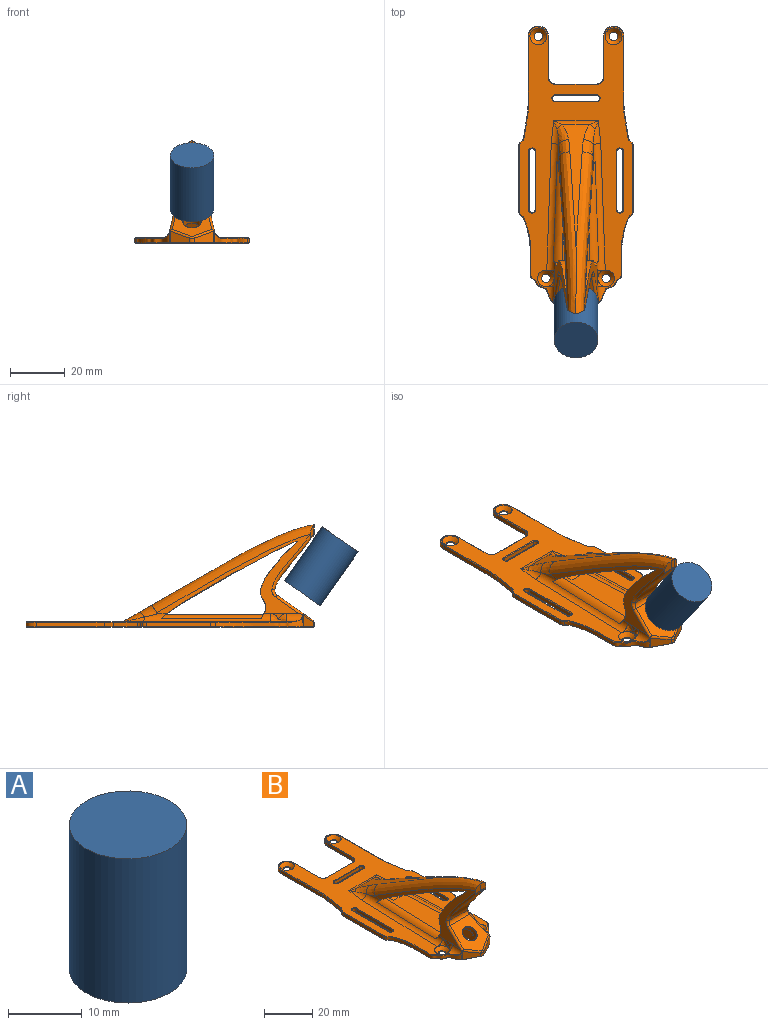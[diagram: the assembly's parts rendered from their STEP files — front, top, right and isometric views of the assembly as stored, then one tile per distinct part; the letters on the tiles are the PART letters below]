
ASSEMBLY  parts=2 mates=1
PART A: 3 faces, bbox 16x16x24 mm
  f0: cylinder r=8mm len=24mm, axis (0,0,-1), area 1206.4mm2, adj f1,f2
  f1: plane 16x16mm, normal (0,0,1), area 201.1mm2, adj f0
  f2: plane 16x16mm, normal (0,0,-1), area 201.1mm2, adj f0
PART B: 226 faces, bbox 42.2x106.4x37.8 mm
  f0: plane 104.85x41.61mm, normal (0,0,-1), area 2882.3mm2, adj f116,f117,f118,f119,f120,f121,f122,f123
  f1: plane 6.09x2.05mm, normal (-1,0.04,0), area 3.8mm2, adj f6,f85
  f2: plane 6.09x2.05mm, normal (1,0.04,0), area 3.8mm2, adj f5,f79
  f3: plane 4.72x2.47mm, normal (-0.46,-0.89,0), area 7mm2, adj f6,f7,f96,f102,f103
  f4: plane 4.71x2.46mm, normal (0.46,-0.89,0), area 7mm2, adj f5,f7,f95,f108,f110
  f5: plane 56.16x28.95mm, normal (0.98,0.03,0.17), area 222.2mm2, adj f2,f4,f76,f77,f78,f80,f94,f95
  f6: plane 56.16x28.95mm, normal (-0.98,0.03,0.17), area 222.2mm2, adj f1,f3,f76,f77,f83,f86,f96,f97
  f7: cylinder r=2mm len=3.6mm, axis (0,0,1), area 6.6mm2, adj f3,f4,f95,f96,f105
  f8: plane 7.11x4.16mm, normal (-0.46,-0.89,0), area 23mm2, adj f61,f62,f109,f150
  f9: plane 7.11x4.16mm, normal (0.46,-0.89,0), area 23mm2, adj f61,f63,f113,f154
  f10: cylinder r=3.15mm len=6.54mm, axis (0,0.57,-0.82), area 47.6mm2, adj f53,f225
  f11: cylinder r=1.1mm len=2.2mm, axis (0,0,-1), area 5.5mm2, adj f12,f45,f173,f222
  f12: plane 15x1.6mm, normal (0,-1,0), area 24mm2, adj f11,f13,f172,f224
  f13: cylinder r=1.1mm len=2.2mm, axis (0,0,-1), area 5.5mm2, adj f12,f45,f174,f223
  f14: cylinder r=1.1mm len=2.2mm, axis (0,0,-1), area 5.5mm2, adj f15,f40,f164,f219
  f15: plane 21.23x1.6mm, normal (1,0,0), area 34mm2, adj f14,f16,f166,f217
  f16: cylinder r=1.1mm len=2.2mm, axis (0,0,-1), area 5.5mm2, adj f15,f40,f167,f218
  f17: cylinder r=1.1mm len=2.2mm, axis (0,0,-1), area 5.5mm2, adj f18,f42,f169,f214
  f18: plane 21.23x1.6mm, normal (-1,0,0), area 34mm2, adj f17,f19,f168,f213
  f19: cylinder r=1.1mm len=2.2mm, axis (0,0,-1), area 5.5mm2, adj f18,f42,f170,f215
  f20: extruded ~32.1x12mm, area 64.2mm2, adj f63,f66,f157,f181,f182
  f21: plane 23.55x1.6mm, normal (1,0,0), area 37.7mm2, adj f66,f67,f153,f184
  f22: plane 1.6x0.89mm, normal (0.74,0.68,0), area 1.9mm2, adj f67,f73,f149,f186
  f23: plane 8.71x1.6mm, normal (0.99,0.16,0), area 14.1mm2, adj f69,f73,f145,f188
  f24: plane 3.14x1.6mm, normal (1,0.08,0), area 5mm2, adj f69,f70,f141,f190
  f25: plane 24.78x1.6mm, normal (1,0,0), area 39.7mm2, adj f26,f70,f137,f192
  f26: cylinder r=3.75mm len=7.5mm, axis (0,0,-1), area 18.8mm2, adj f25,f27,f135,f193
  f27: plane 14.86x1.6mm, normal (-1,0,0), area 23.8mm2, adj f26,f28,f133,f194
  f28: cylinder r=2.61mm len=2.61mm, axis (0,0,-1), area 6.6mm2, adj f27,f29,f131,f195
  f29: plane 14.78x1.6mm, normal (0,1,0), area 23.7mm2, adj f28,f30,f129,f196
  f30: cylinder r=2.61mm len=2.61mm, axis (0,0,-1), area 6.6mm2, adj f29,f31,f127,f197
  f31: plane 14.86x1.6mm, normal (1,0,0), area 23.8mm2, adj f30,f32,f125,f198
  f32: cylinder r=3.75mm len=7.5mm, axis (0,0,-1), area 18.8mm2, adj f31,f33,f124,f199
  f33: plane 24.78x1.6mm, normal (-1,0,0), area 39.7mm2, adj f32,f71,f126,f200
  f34: plane 3.14x1.6mm, normal (-1,0.08,0), area 5mm2, adj f71,f72,f130,f202
  f35: plane 8.71x1.6mm, normal (-0.99,0.16,0), area 14.1mm2, adj f68,f72,f134,f204
  f36: plane 1.6x0.89mm, normal (-0.74,0.68,0), area 1.9mm2, adj f64,f68,f138,f206
  f37: plane 23.55x1.6mm, normal (-1,0,0), area 37.7mm2, adj f64,f65,f142,f208
  f38: cylinder r=1.57mm len=3.15mm, axis (0,0,-1), area 3mm2, adj f59,f177
  f39: cylinder r=1.57mm len=3.15mm, axis (0,0,-1), area 3mm2, adj f58,f176
  f40: plane 21.23x1.6mm, normal (-1,0,0), area 34mm2, adj f14,f16,f165,f220
  f41: cylinder r=1.55mm len=3.1mm, axis (0,0,-1), area 2.9mm2, adj f56,f178
  f42: plane 21.23x1.6mm, normal (1,0,0), area 34mm2, adj f17,f19,f171,f216
  f43: cylinder r=1.55mm len=3.1mm, axis (0,0,-1), area 2.9mm2, adj f57,f179
  f44: extruded ~32.1x12mm, area 64.2mm2, adj f62,f65,f146,f210,f211
  f45: plane 15x1.6mm, normal (0,1,0), area 24mm2, adj f11,f13,f175,f221
  f46: plane 96x41.6mm, normal (0,0,1), area 1596.5mm2, adj f56,f57,f58,f59,f78,f80,f81,f82
  f47: plane 8.66x7.62mm, normal (0.87,-0.41,-0.29), area 37mm2, adj f48,f52,f53,f162,f163
  f48: plane 7.68x5.38mm, normal (0,-0.82,-0.57), area 43.9mm2, adj f47,f49,f53,f159,f161,f163
  f49: plane 8.66x7.62mm, normal (-0.87,-0.41,-0.29), area 37mm2, adj f48,f50,f53,f158,f159
  f50: plane 6.95x5.18mm, normal (-0.87,0.41,0.29), area 23mm2, adj f49,f51,f53,f158,f160
  f51: plane 4.69x2.79mm, normal (0,0.82,0.57), area 16mm2, adj f50,f52,f53,f160
  f52: plane 6.95x5.18mm, normal (0.87,0.41,0.29), area 23mm2, adj f47,f51,f53,f160,f162
  f53: plane 9.38x6.65mm, normal (0,0.57,-0.82), area 25.9mm2, adj f10,f47,f48,f49,f50,f51,f52
  f54: extruded ~19.58x13.98mm, area 169.4mm2, adj f60,f102,f103,f105,f108,f110
  f55: plane 14.42x13.09mm, normal (0,-0.57,0.82), area 147mm2, adj f60,f107,f109,f111,f113,f114,f225
  f56: cone r=1.55mm half-angle=45deg, axis (0,0,1), area 30.7mm2, adj f41,f46,f79
  f57: cone r=1.55mm half-angle=45deg, axis (0,0,1), area 30.7mm2, adj f43,f46,f85
  f58: cone r=3.08mm half-angle=45deg, axis (0,0,1), area 31mm2, adj f39,f46
  f59: cone r=1.57mm half-angle=45deg, axis (0,0,1), area 31mm2, adj f38,f46
  f60: cylinder r=2mm len=11.41mm, axis (1,0,0), area 23.5mm2, adj f54,f55,f104,f112
  f61: cylinder r=2mm len=1.84mm, axis (0,0,1), area 3mm2, adj f8,f9,f111,f152
  f62: cylinder r=2mm len=4.16mm, axis (0,0,-1), area 1.2mm2, adj f8,f44,f106,f148,f212
  f63: cylinder r=2mm len=4.16mm, axis (0,0,-1), area 1.2mm2, adj f9,f20,f115,f156,f180
  f64: cylinder r=2mm len=1.6mm, axis (0,0,1), area 2.4mm2, adj f36,f37,f140,f207
  f65: cylinder r=2mm len=1.6mm, axis (0,0,-1), area 2.8mm2, adj f37,f44,f144,f209
  f66: cylinder r=2mm len=1.6mm, axis (0,0,-1), area 2.8mm2, adj f20,f21,f155,f183
  f67: cylinder r=2mm len=1.6mm, axis (0,0,-1), area 2.4mm2, adj f21,f22,f151,f185
  f68: cylinder r=2mm len=1.6mm, axis (0,0,1), area 1.9mm2, adj f35,f36,f136,f205
  f69: cylinder r=2mm len=1.6mm, axis (0,0,1), area 0.3mm2, adj f23,f24,f143,f189
  f70: cylinder r=2mm len=1.6mm, axis (0,0,1), area 0.2mm2, adj f24,f25,f139,f191
  f71: cylinder r=2mm len=1.6mm, axis (0,0,1), area 0.2mm2, adj f33,f34,f128,f201
  f72: cylinder r=2mm len=1.6mm, axis (0,0,1), area 0.3mm2, adj f34,f35,f132,f203
  f73: cylinder r=2mm len=1.6mm, axis (0,0,1), area 1.9mm2, adj f22,f23,f147,f187
  f74: extruded ~44.51x25.33mm, area 163.2mm2, adj f82,f93,f94,f95,f96,f97,f98
  f75: plane 35.61x10.28mm, normal (0,0,1), area 300.5mm2, adj f76,f77,f88,f90,f91,f100,f101
  f76: extruded ~28.33x16.46mm, area 345mm2, adj f5,f6,f75,f77,f80,f86,f100,f101
  f77: extruded ~49.67x28.33mm, area 519.4mm2, adj f5,f6,f75,f76,f80,f86,f89,f90
  f78: cylinder r=3mm len=5.88mm, axis (-0.04,1,0), area 19.9mm2, adj f5,f46,f79,f114,f180,f181
  f79: bspline ~6.79x3.25mm, area 16.8mm2, adj f2,f56,f78,f80
  f80: cylinder r=3mm len=46.28mm, axis (-0.04,1,0), area 141mm2, adj f5,f46,f76,f77,f79,f81,f94,f100
  f81: cylinder r=3mm len=8.78mm, axis (-0.11,0.99,0), area 16.2mm2, adj f46,f80,f92,f93,f94
  f82: cylinder r=3mm len=16.24mm, axis (1,0,0), area 19.6mm2, adj f46,f74,f92,f99
  f83: cylinder r=3mm len=5.88mm, axis (-0.04,-1,0), area 19.9mm2, adj f6,f46,f85,f107,f211,f212
  f84: cylinder r=3mm len=8.78mm, axis (-0.11,-0.99,0), area 16.2mm2, adj f46,f86,f97,f98,f99
  f85: bspline ~6.79x3.25mm, area 16.8mm2, adj f1,f57,f83,f86
  f86: cylinder r=3mm len=46.28mm, axis (-0.04,-1,0), area 141mm2, adj f6,f46,f76,f77,f84,f85,f97,f101
  f87: cylinder r=3.77mm len=7.52mm, axis (1,0,0), area 57mm2, adj f90,f91,f119,f123
  f88: cylinder r=5.77mm len=5.01mm, axis (1,0,0), area 25.8mm2, adj f75,f90,f91,f120,f121,f122
  f89: cylinder r=5.77mm len=6.38mm, axis (1,0,0), area 47.4mm2, adj f77,f90,f91,f116,f117,f118
  f90: plane 11.52x5.57mm, normal (1,0,0), area 26.4mm2, adj f75,f77,f87,f88,f89,f117,f119,f122
  f91: plane 11.52x5.57mm, normal (-1,0,0), area 26.4mm2, adj f75,f77,f87,f88,f89,f118,f119,f121
  f92: bspline ~3.82x3.65mm, area 2.5mm2, adj f81,f82,f93
  f93: bspline ~9.06x4.61mm, area 21.9mm2, adj f74,f81,f92,f94
  f94: bspline ~9.19x5.76mm, area 26.3mm2, adj f5,f74,f80,f81,f93,f95
  f95: bspline ~61.44x33.07mm, area 351mm2, adj f4,f5,f7,f74,f94,f96
  f96: bspline ~64.06x34.52mm, area 351mm2, adj f3,f6,f7,f74,f95,f97
  f97: bspline ~9.19x5.76mm, area 26.3mm2, adj f6,f74,f84,f86,f96,f98
  f98: bspline ~9.06x4.61mm, area 21.9mm2, adj f74,f84,f97,f99
  f99: bspline ~3.82x3.65mm, area 2.5mm2, adj f82,f84,f98
  f100: cylinder r=4mm len=37.15mm, axis (-0.04,1,0), area 128.4mm2, adj f75,f76,f77,f80
  f101: cylinder r=4mm len=37.15mm, axis (-0.04,-1,0), area 128.4mm2, adj f75,f76,f77,f86
  f102: bspline ~21.26x15.46mm, area 40.2mm2, adj f3,f6,f54,f103,f104
  f103: bspline ~5.15x3.44mm, area 2mm2, adj f3,f54,f102,f105
  f104: bspline ~2.81x1.89mm, area 4mm2, adj f6,f60,f102,f107
  f105: bspline ~2.6x0.93mm, area 1.2mm2, adj f7,f54,f103,f108
  f106: bspline ~0.3x0.17mm, area 0mm2, adj f62,f107,f109,f212
  f107: cylinder r=1mm len=10.49mm, axis (-0.13,-0.81,-0.57), area 17mm2, adj f6,f55,f83,f104,f106,f109,f212
  f108: bspline ~5.15x3.44mm, area 2mm2, adj f4,f54,f105,f110
  f109: cylinder r=1mm len=7.57mm, axis (-0.84,0.44,0.31), area 8.6mm2, adj f8,f55,f106,f107,f111
  f110: bspline ~21.26x15.46mm, area 40.2mm2, adj f4,f5,f54,f108,f112
  f111: bspline ~1.84x0.9mm, area 1.5mm2, adj f55,f61,f109,f113
  f112: bspline ~2.81x1.89mm, area 4mm2, adj f5,f60,f110,f114
  f113: cylinder r=1mm len=7.57mm, axis (-0.84,-0.44,-0.31), area 8.6mm2, adj f9,f55,f111,f114,f115
  f114: cylinder r=1mm len=10.49mm, axis (0.13,-0.81,-0.57), area 17mm2, adj f5,f55,f78,f112,f113,f115,f180
  f115: bspline ~0.3x0.17mm, area 0mm2, adj f63,f113,f114,f180
  f116: plane 5.4x0.2mm, normal (0,-0.7,-0.72), area 1.4mm2, adj f0,f89,f117,f118
  f117: plane 2.4x0.2mm, normal (0.71,0,-0.71), area 0.6mm2, adj f0,f89,f90,f116,f119
  f118: plane 2.4x0.2mm, normal (-0.71,0,-0.71), area 0.6mm2, adj f0,f89,f91,f116,f119
  f119: plane 5.4x0.21mm, normal (0,0.73,-0.69), area 1.5mm2, adj f0,f87,f90,f91,f117,f118
  f120: plane 5.4x0.2mm, normal (0,0.7,-0.72), area 1.4mm2, adj f0,f88,f121,f122
  f121: plane 2.4x0.2mm, normal (-0.71,0,-0.71), area 0.6mm2, adj f0,f88,f91,f120,f123
  f122: plane 2.4x0.2mm, normal (0.71,0,-0.71), area 0.6mm2, adj f0,f88,f90,f120,f123
  f123: plane 5.4x0.21mm, normal (0,-0.73,-0.69), area 1.5mm2, adj f0,f87,f90,f91,f121,f122
  f124: cone r=3.75mm half-angle=45deg, axis (0,0,1), area 3.2mm2, adj f0,f32,f125,f126
  f125: plane 14.86x0.2mm, normal (0.71,0,-0.71), area 4.2mm2, adj f0,f31,f124,f127
  f126: plane 24.78x0.2mm, normal (-0.71,0,-0.71), area 7mm2, adj f0,f33,f124,f128
  f127: cone r=2.81mm half-angle=45deg, axis (0,0,-1), area 1.2mm2, adj f0,f30,f125,f129
  f128: cone r=2.2mm half-angle=45deg, axis (0,0,-1), area 0mm2, adj f0,f71,f126,f130
  f129: plane 14.78x0.2mm, normal (0,0.71,-0.71), area 4.2mm2, adj f0,f29,f127,f131
  f130: plane 3.16x0.44mm, normal (-0.71,0.05,-0.71), area 0.9mm2, adj f0,f34,f128,f132
  f131: cone r=2.81mm half-angle=45deg, axis (0,0,-1), area 1.2mm2, adj f0,f28,f129,f133
  f132: cone r=2.2mm half-angle=45deg, axis (0,0,-1), area 0mm2, adj f0,f72,f130,f134
  f133: plane 14.86x0.2mm, normal (-0.71,0,-0.71), area 4.2mm2, adj f0,f27,f131,f135
  f134: plane 8.74x1.58mm, normal (-0.7,0.11,-0.71), area 2.5mm2, adj f0,f35,f132,f136
  f135: cone r=3.55mm half-angle=45deg, axis (0,0,1), area 3.2mm2, adj f0,f26,f133,f137
  f136: cone r=2.2mm half-angle=45deg, axis (0,0,-1), area 0.3mm2, adj f0,f68,f134,f138
  f137: plane 24.78x0.2mm, normal (0.71,0,-0.71), area 7mm2, adj f0,f25,f135,f139
  f138: plane 1.02x0.96mm, normal (-0.52,0.48,-0.71), area 0.3mm2, adj f0,f36,f136,f140
  f139: cone r=2.2mm half-angle=45deg, axis (0,0,-1), area 0mm2, adj f0,f70,f137,f141
  f140: cone r=1.8mm half-angle=45deg, axis (0,0,1), area 0.4mm2, adj f0,f64,f138,f142
  f141: plane 3.16x0.44mm, normal (0.71,0.05,-0.71), area 0.9mm2, adj f0,f24,f139,f143
  f142: plane 23.55x0.2mm, normal (-0.71,0,-0.71), area 6.7mm2, adj f0,f37,f140,f144
  f143: cone r=2.2mm half-angle=45deg, axis (0,0,-1), area 0mm2, adj f0,f69,f141,f145
  f144: cone r=1.8mm half-angle=45deg, axis (0,0,1), area 0.5mm2, adj f0,f65,f142,f146
  f145: plane 8.74x1.58mm, normal (0.7,0.11,-0.71), area 2.5mm2, adj f0,f23,f143,f147
  f146: bspline ~32.26x12.12mm, area 10.3mm2, adj f0,f44,f144,f148
  f147: cone r=2.2mm half-angle=45deg, axis (0,0,-1), area 0.3mm2, adj f0,f73,f145,f149
  f148: cone r=1.8mm half-angle=45deg, axis (0,0,1), area 0.1mm2, adj f0,f62,f146,f150
  f149: plane 1.02x0.96mm, normal (0.52,0.48,-0.71), area 0.3mm2, adj f0,f22,f147,f151
  f150: plane 7.2x3.87mm, normal (-0.33,-0.63,-0.71), area 2.3mm2, adj f0,f8,f148,f152
  f151: cone r=1.8mm half-angle=45deg, axis (0,0,1), area 0.4mm2, adj f0,f67,f149,f153
  f152: cone r=1.8mm half-angle=45deg, axis (0,0,1), area 0.5mm2, adj f0,f61,f150,f154
  f153: plane 23.55x0.2mm, normal (0.71,0,-0.71), area 6.7mm2, adj f0,f21,f151,f155
  f154: plane 7.2x3.87mm, normal (0.33,-0.63,-0.71), area 2.3mm2, adj f0,f9,f152,f156
  f155: cone r=1.8mm half-angle=45deg, axis (0,0,1), area 0.5mm2, adj f0,f66,f153,f157
  f156: cone r=1.8mm half-angle=45deg, axis (0,0,1), area 0.1mm2, adj f0,f63,f154,f157
  f157: bspline ~32.26x12.12mm, area 10.3mm2, adj f0,f20,f155,f156
  f158: plane 5.2x2.61mm, normal (-0.73,0.34,-0.6), area 1.8mm2, adj f0,f49,f50,f159,f160
  f159: plane 5.3x2.58mm, normal (-0.54,-0.26,-0.8), area 1.4mm2, adj f0,f48,f49,f158,f161
  f160: plane 4.92x0.31mm, normal (0,0.89,-0.46), area 1.7mm2, adj f0,f50,f51,f52,f158,f162
  f161: plane 4.92x0.16mm, normal (0,-0.46,-0.89), area 0.9mm2, adj f0,f48,f159,f163
  f162: plane 5.2x2.61mm, normal (0.73,0.34,-0.6), area 1.8mm2, adj f0,f47,f52,f160,f163
  f163: plane 5.3x2.58mm, normal (0.54,-0.26,-0.8), area 1.4mm2, adj f0,f47,f48,f161,f162
  f164: cone r=1.3mm half-angle=45deg, axis (0,0,-1), area 1.1mm2, adj f0,f14,f165,f166
  f165: plane 21.23x0.2mm, normal (-0.71,0,-0.71), area 6mm2, adj f0,f40,f164,f167
  f166: plane 21.23x0.2mm, normal (0.71,0,-0.71), area 6mm2, adj f0,f15,f164,f167
  f167: cone r=1.3mm half-angle=45deg, axis (0,0,-1), area 1.1mm2, adj f0,f16,f165,f166
  f168: plane 21.23x0.2mm, normal (-0.71,0,-0.71), area 6mm2, adj f0,f18,f169,f170
  f169: cone r=1.1mm half-angle=45deg, axis (0,0,-1), area 1.1mm2, adj f0,f17,f168,f171
  f170: cone r=1.1mm half-angle=45deg, axis (0,0,-1), area 1.1mm2, adj f0,f19,f168,f171
  f171: plane 21.23x0.2mm, normal (0.71,0,-0.71), area 6mm2, adj f0,f42,f169,f170
  f172: plane 15x0.2mm, normal (0,-0.71,-0.71), area 4.2mm2, adj f0,f12,f173,f174
  f173: cone r=1.1mm half-angle=45deg, axis (0,0,-1), area 1.1mm2, adj f0,f11,f172,f175
  f174: cone r=1.1mm half-angle=45deg, axis (0,0,-1), area 1.1mm2, adj f0,f13,f172,f175
  f175: plane 15x0.2mm, normal (0,0.71,-0.71), area 4.2mm2, adj f0,f45,f173,f174
  f176: cone r=1.57mm half-angle=45deg, axis (0,0,-1), area 3mm2, adj f0,f39
  f177: cone r=1.78mm half-angle=45deg, axis (0,0,-1), area 3mm2, adj f0,f38
  f178: cone r=1.75mm half-angle=45deg, axis (0,0,-1), area 2.9mm2, adj f0,f41
  f179: cone r=1.75mm half-angle=45deg, axis (0,0,-1), area 2.9mm2, adj f0,f43
  f180: bspline ~0.82x0.33mm, area 0.2mm2, adj f63,f78,f114,f115,f181
  f181: bspline ~4.97x2.79mm, area 1.4mm2, adj f20,f78,f180,f182
  f182: bspline ~27.42x9.35mm, area 8.7mm2, adj f20,f46,f181,f183
  f183: cone r=1.8mm half-angle=45deg, axis (0,0,-1), area 0.5mm2, adj f46,f66,f182,f184
  f184: plane 23.55x0.2mm, normal (0.71,0,0.71), area 6.7mm2, adj f21,f46,f183,f185
  f185: cone r=1.8mm half-angle=45deg, axis (0,0,-1), area 0.4mm2, adj f46,f67,f184,f186
  f186: plane 1.02x0.96mm, normal (0.52,0.48,0.71), area 0.3mm2, adj f22,f46,f185,f187
  f187: cone r=2.2mm half-angle=45deg, axis (0,0,1), area 0.3mm2, adj f46,f73,f186,f188
  f188: plane 8.74x1.58mm, normal (0.7,0.11,0.71), area 2.5mm2, adj f23,f46,f187,f189
  f189: cone r=2.2mm half-angle=45deg, axis (0,0,1), area 0mm2, adj f46,f69,f188,f190
  f190: plane 3.16x0.44mm, normal (0.71,0.05,0.71), area 0.9mm2, adj f24,f46,f189,f191
  f191: cone r=2.2mm half-angle=45deg, axis (0,0,1), area 0mm2, adj f46,f70,f190,f192
  f192: plane 24.78x0.2mm, normal (0.71,0,0.71), area 7mm2, adj f25,f46,f191,f193
  f193: cone r=3.75mm half-angle=45deg, axis (0,0,-1), area 3.2mm2, adj f26,f46,f192,f194
  f194: plane 14.86x0.2mm, normal (-0.71,0,0.71), area 4.2mm2, adj f27,f46,f193,f195
  f195: cone r=2.61mm half-angle=45deg, axis (0,0,1), area 1.2mm2, adj f28,f46,f194,f196
  f196: plane 14.78x0.2mm, normal (0,0.71,0.71), area 4.2mm2, adj f29,f46,f195,f197
  f197: cone r=2.61mm half-angle=45deg, axis (0,0,1), area 1.2mm2, adj f30,f46,f196,f198
  f198: plane 14.86x0.2mm, normal (0.71,0,0.71), area 4.2mm2, adj f31,f46,f197,f199
  f199: cone r=3.55mm half-angle=45deg, axis (0,0,-1), area 3.2mm2, adj f32,f46,f198,f200
  f200: plane 24.78x0.2mm, normal (-0.71,0,0.71), area 7mm2, adj f33,f46,f199,f201
  f201: cone r=2.2mm half-angle=45deg, axis (0,0,1), area 0mm2, adj f46,f71,f200,f202
  f202: plane 3.16x0.44mm, normal (-0.71,0.05,0.71), area 0.9mm2, adj f34,f46,f201,f203
  f203: cone r=2.2mm half-angle=45deg, axis (0,0,1), area 0mm2, adj f46,f72,f202,f204
  f204: plane 8.74x1.58mm, normal (-0.7,0.11,0.71), area 2.5mm2, adj f35,f46,f203,f205
  f205: cone r=2.2mm half-angle=45deg, axis (0,0,1), area 0.3mm2, adj f46,f68,f204,f206
  f206: plane 1.02x0.96mm, normal (-0.52,0.48,0.71), area 0.3mm2, adj f36,f46,f205,f207
  f207: cone r=1.8mm half-angle=45deg, axis (0,0,-1), area 0.4mm2, adj f46,f64,f206,f208
  f208: plane 23.55x0.2mm, normal (-0.71,0,0.71), area 6.7mm2, adj f37,f46,f207,f209
  f209: cone r=1.8mm half-angle=45deg, axis (0,0,-1), area 0.5mm2, adj f46,f65,f208,f210
  f210: bspline ~27.42x9.35mm, area 8.7mm2, adj f44,f46,f209,f211
  f211: bspline ~4.97x2.79mm, area 1.4mm2, adj f44,f83,f210,f212
  f212: bspline ~0.82x0.33mm, area 0.2mm2, adj f62,f83,f106,f107,f211
  f213: plane 21.23x0.2mm, normal (-0.71,0,0.71), area 6mm2, adj f18,f46,f214,f215
  f214: cone r=1.3mm half-angle=45deg, axis (0,0,1), area 1.1mm2, adj f17,f46,f213,f216
  f215: cone r=1.3mm half-angle=45deg, axis (0,0,1), area 1.1mm2, adj f19,f46,f213,f216
  f216: plane 21.23x0.2mm, normal (0.71,0,0.71), area 6mm2, adj f42,f46,f214,f215
  f217: plane 21.23x0.2mm, normal (0.71,0,0.71), area 6mm2, adj f15,f46,f218,f219
  f218: cone r=1.1mm half-angle=45deg, axis (0,0,1), area 1.1mm2, adj f16,f46,f217,f220
  f219: cone r=1.1mm half-angle=45deg, axis (0,0,1), area 1.1mm2, adj f14,f46,f217,f220
  f220: plane 21.23x0.2mm, normal (-0.71,0,0.71), area 6mm2, adj f40,f46,f218,f219
  f221: plane 15x0.2mm, normal (0,0.71,0.71), area 4.2mm2, adj f45,f46,f222,f223
  f222: cone r=1.3mm half-angle=45deg, axis (0,0,1), area 1.1mm2, adj f11,f46,f221,f224
  f223: cone r=1.3mm half-angle=45deg, axis (0,0,1), area 1.1mm2, adj f13,f46,f221,f224
  f224: plane 15x0.2mm, normal (0,-0.71,0.71), area 4.2mm2, adj f12,f46,f222,f223
  f225: cone r=3.35mm half-angle=45deg, axis (0,-0.57,0.82), area 5.8mm2, adj f10,f55
PLACE A rot(axis=(1,0,0),35deg) t=(-28.68,-43.36,25.21)mm
PLACE B t=(-28.68,-10.85,12.79)mm fixed
MATE slider A.f0 <-> B.f10  axis (0,0.57,-0.82) through (-28.68,-43.36,25.21)mm
